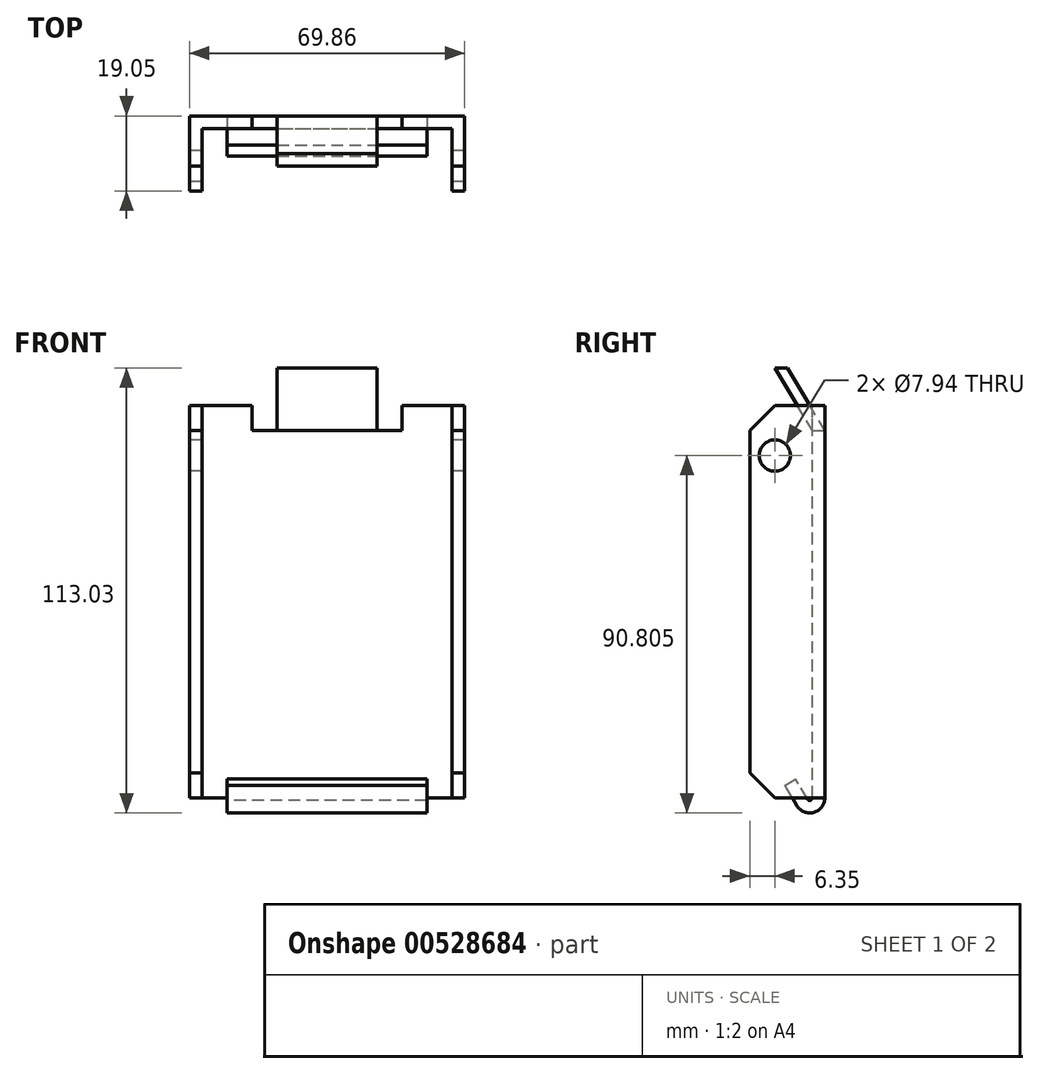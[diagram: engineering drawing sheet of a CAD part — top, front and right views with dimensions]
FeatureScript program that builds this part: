
annotation { "Feature Type Name" : "Feature", "Feature Type Description" : "" }
export const myFeature = defineFeature(function(context is Context, id is Id, definition is map)
    precondition{}
    {
        {
            var Q0;
            Q0=qCreatedBy(makeId("Front.planeOp"),FACE);
            var sketch = newSketch(context, id + "F0", { "sketchPlane" : qUnion([Q0])});
            skLineSegment(sketch, "E0.bottom", {"start": v(0, 0) * mm, "end": v(63.5, 0) * mm});
            skLineSegment(sketch, "E0.left", {"start": v(0, 0) * mm, "end": v(0, 99.7) * mm});
            skLineSegment(sketch, "E0.right", {"start": v(63.5, 0) * mm, "end": v(63.5, 99.7) * mm});
            skLineSegment(sketch, "E1", {"start": v(0, 99.7) * mm, "end": v(12.7, 99.7) * mm});
            skLineSegment(sketch, "E2", {"start": v(12.7, 99.7) * mm, "end": v(12.7, 93.34) * mm});
            skLineSegment(sketch, "E3", {"start": v(12.7, 93.35) * mm, "end": v(50.8, 93.35) * mm});
            skLineSegment(sketch, "E4", {"start": v(50.8, 93.35) * mm, "end": v(50.8, 99.7) * mm});
            skLineSegment(sketch, "E5", {"start": v(50.8, 99.7) * mm, "end": v(63.5, 99.7) * mm});
            skSolve(sketch);
        }
        {
            var Q0;
            Q0 = qSketchRegion(id + "F0", true);
            extrude(context, id + "F1", {"entities" : qUnion([Q0]), "depth" : 3.17 * mm, "offsetDistance" : 25.4 * mm});
        }
        {
            var Q0;
            Q0=qCreatedBy(makeId("Right.planeOp"),FACE);
            var sketch = newSketch(context, id + "F2", { "sketchPlane" : qUnion([Q0])});
            skLineSegment(sketch, "E6", {"start": v(0, 0) * mm, "end": v(0, 99.7) * mm});
            skLineSegment(sketch, "E7", {"start": v(0, 99.7) * mm, "end": v(-12.7, 99.7) * mm});
            skLineSegment(sketch, "E8", {"start": v(-12.7, 99.7) * mm, "end": v(-19.05, 93.35) * mm});
            skLineSegment(sketch, "E9", {"start": v(-19.05, 93.35) * mm, "end": v(-19.05, 6.35) * mm});
            skLineSegment(sketch, "E10", {"start": v(-19.05, 6.35) * mm, "end": v(-12.7, 0) * mm});
            skLineSegment(sketch, "E11", {"start": v(-12.7, 0) * mm, "end": v(0, 0) * mm});
            skSolve(sketch);
        }
        {
            var Q0;
            Q0=makeQuery(id+"F2.imprint","IMPRINT",FACE,{"disambiguationData":[TD([[makeQuery(id+"F2.imprint","IMPRINT",EDGE,{"derivedFrom":sQuery(id+"F2.wireOp",EDGE,"E6")}),1.0]])]});
            extrude(context, id + "F3", {"entities" : qUnion([Q0]), "operationType" : NewBodyOperationType.ADD, "oppositeDirection" : true, "depth" : 3.17 * mm, "offsetDistance" : 25.4 * mm});
        }
        {
            var Q0;
            Q0=makeQuery(id+"F1.opExtrude","SWEPT_FACE",FACE,{"disambiguationData":[OSD([sQuery(id+"F0.wireOp",EDGE,"E0.right")])]});
            var sketch = newSketch(context, id + "F4", { "sketchPlane" : qUnion([Q0])});
            skLineSegment(sketch, "E12", {"start": v(0, 0) * mm, "end": v(0, 99.7) * mm});
            skLineSegment(sketch, "E13", {"start": v(0, 99.7) * mm, "end": v(-12.7, 99.7) * mm});
            skLineSegment(sketch, "E14", {"start": v(-12.7, 99.7) * mm, "end": v(-19.05, 93.34) * mm});
            skLineSegment(sketch, "E15", {"start": v(-19.05, 93.34) * mm, "end": v(-19.05, 6.35) * mm});
            skLineSegment(sketch, "E16", {"start": v(-19.05, 6.35) * mm, "end": v(-12.7, 0) * mm});
            skLineSegment(sketch, "E17", {"start": v(-12.7, 0) * mm, "end": v(0, 0) * mm});
            skSolve(sketch);
        }
        {
            var Q0;
            Q0 = qSketchRegion(id + "F4", true);
            extrude(context, id + "F5", {"entities" : qUnion([Q0]), "operationType" : NewBodyOperationType.ADD, "depth" : 3.17 * mm, "offsetDistance" : 25.4 * mm});
        }
        {
            var Q0;
            Q0=makeQuery(id+"F5.boolean.opBoolean","MERGE",FACE,{"derivedFrom":[makeQuery(id+"F3.boolean.opBoolean","MERGE",FACE,{"derivedFrom":[makeQuery(id+"F1.opExtrude","SWEPT_FACE",FACE,{"disambiguationData":[OSD([sQuery(id+"F0.wireOp",EDGE,"E0.bottom")])]}),makeQuery(id+"F3.opExtrude","SWEPT_FACE",FACE,{"disambiguationData":[OSD([sQuery(id+"F2.wireOp",EDGE,"E11")])]})]}),makeQuery(id+"F5.opExtrude","SWEPT_FACE",FACE,{"disambiguationData":[OSD([sQuery(id+"F4.wireOp",EDGE,"E17")])]})]});
            var sketch = newSketch(context, id + "F6", { "sketchPlane" : qUnion([Q0])});
            skLineSegment(sketch, "E18.bottom", {"start": v(57.15, 0) * mm, "end": v(6.35, 0) * mm});
            skLineSegment(sketch, "E18.top", {"start": v(57.15, 3.18) * mm, "end": v(6.35, 3.18) * mm});
            skLineSegment(sketch, "E18.left", {"start": v(57.15, 0) * mm, "end": v(57.15, 3.18) * mm});
            skLineSegment(sketch, "E18.right", {"start": v(6.35, 0) * mm, "end": v(6.35, 3.18) * mm});
            skSolve(sketch);
        }
        {
            var Q0;
            Q0=qCreatedBy(makeId("Right.planeOp"),FACE);
            var sketch = newSketch(context, id + "F7", { "sketchPlane" : qUnion([Q0])});
            skArc(sketch, "E19", {"start": v(-7.08, -1.96) * mm, "mid": v(-2.8, -3.67) * mm, "end": v(0, 0) * mm});
            skLineSegment(sketch, "E20", {"start": v(-7.08, -1.96) * mm, "end": v(-10.16, 3.18) * mm});
            skSolve(sketch);
        }
        {
            var Q0;
            Q0=makeQuery(id+"F6.imprint","IMPRINT",FACE,{"disambiguationData":[TD([[makeQuery(id+"F6.imprint","IMPRINT",EDGE,{"derivedFrom":sQuery(id+"F6.wireOp",EDGE,"E18.bottom")}),1.0]])]});
            var Q1;
            Q1=sQuery(id+"F7.wireOp",EDGE,"E19");
            var Q2;
            Q2=sQuery(id+"F7.wireOp",EDGE,"E20");
            sweep(context, id + "F8", {"operationType" : NewBodyOperationType.ADD, "profiles" : qUnion([Q0]), "path" : qUnion([Q1, Q2])});
        }
        {
            var Q0;
            Q0=makeQuery(id+"F1.opExtrude","SWEPT_FACE",FACE,{"disambiguationData":[OSD([sQuery(id+"F0.wireOp",EDGE,"E3")])]});
            var sketch = newSketch(context, id + "F9", { "sketchPlane" : qUnion([Q0])});
            skLineSegment(sketch, "E21.bottom", {"start": v(19.05, -3.18) * mm, "end": v(44.45, -3.18) * mm});
            skLineSegment(sketch, "E21.top", {"start": v(19.05, 0) * mm, "end": v(44.45, 0) * mm});
            skLineSegment(sketch, "E21.left", {"start": v(19.05, -3.18) * mm, "end": v(19.05, 0) * mm});
            skLineSegment(sketch, "E21.right", {"start": v(44.45, -3.17) * mm, "end": v(44.45, 0) * mm});
            skSolve(sketch);
        }
        {
            var Q0;
            Q0=qCreatedBy(makeId("Right.planeOp"),FACE);
            var sketch = newSketch(context, id + "F10", { "sketchPlane" : qUnion([Q0])});
            skLineSegment(sketch, "E22", {"start": v(-3.17, 93.35) * mm, "end": v(-12.7, 109.22) * mm});
            skSolve(sketch);
        }
        {
            var Q0;
            Q0=makeQuery(id+"F9.imprint","IMPRINT",FACE,{"disambiguationData":[TD([[makeQuery(id+"F9.imprint","IMPRINT",EDGE,{"derivedFrom":sQuery(id+"F9.wireOp",EDGE,"E21.bottom")}),1.0]])]});
            var Q1;
            Q1=sQuery(id+"F10.wireOp",EDGE,"E22");
            sweep(context, id + "F11", {"operationType" : NewBodyOperationType.ADD, "profiles" : qUnion([Q0]), "path" : qUnion([Q1])});
        }
        {
            var Q0;
            Q0=makeQuery(id+"F3.opExtrude","CAP_FACE",FACE,{"disambiguationData":[OSD([sQuery(id+"F2.wireOp",EDGE,"E6"),sQuery(id+"F2.wireOp",EDGE,"E7"),sQuery(id+"F2.wireOp",EDGE,"E8"),sQuery(id+"F2.wireOp",EDGE,"E9"),sQuery(id+"F2.wireOp",EDGE,"E10"),sQuery(id+"F2.wireOp",EDGE,"E11")])],"isStart":false});
            var sketch = newSketch(context, id + "F12", { "sketchPlane" : qUnion([Q0])});
            skCircle(sketch, "E23", {"center": v(12.7, 87) * mm, "radius": 3.97 * mm});
            skSolve(sketch);
        }
        {
            var Q0;
            Q0=makeQuery(id+"F12.imprint","IMPRINT",FACE,{"disambiguationData":[TD([[makeQuery(id+"F12.imprint","IMPRINT",EDGE,{"derivedFrom":sQuery(id+"F12.wireOp",EDGE,"E23")}),1.0]])]});
            extrude(context, id + "F13", {"entities" : qUnion([Q0]), "operationType" : NewBodyOperationType.REMOVE, "endBound" : BoundingType.THROUGH_ALL, "oppositeDirection" : true, "depth" : 25.4 * mm, "offsetDistance" : 25.4 * mm});
        }
    });
